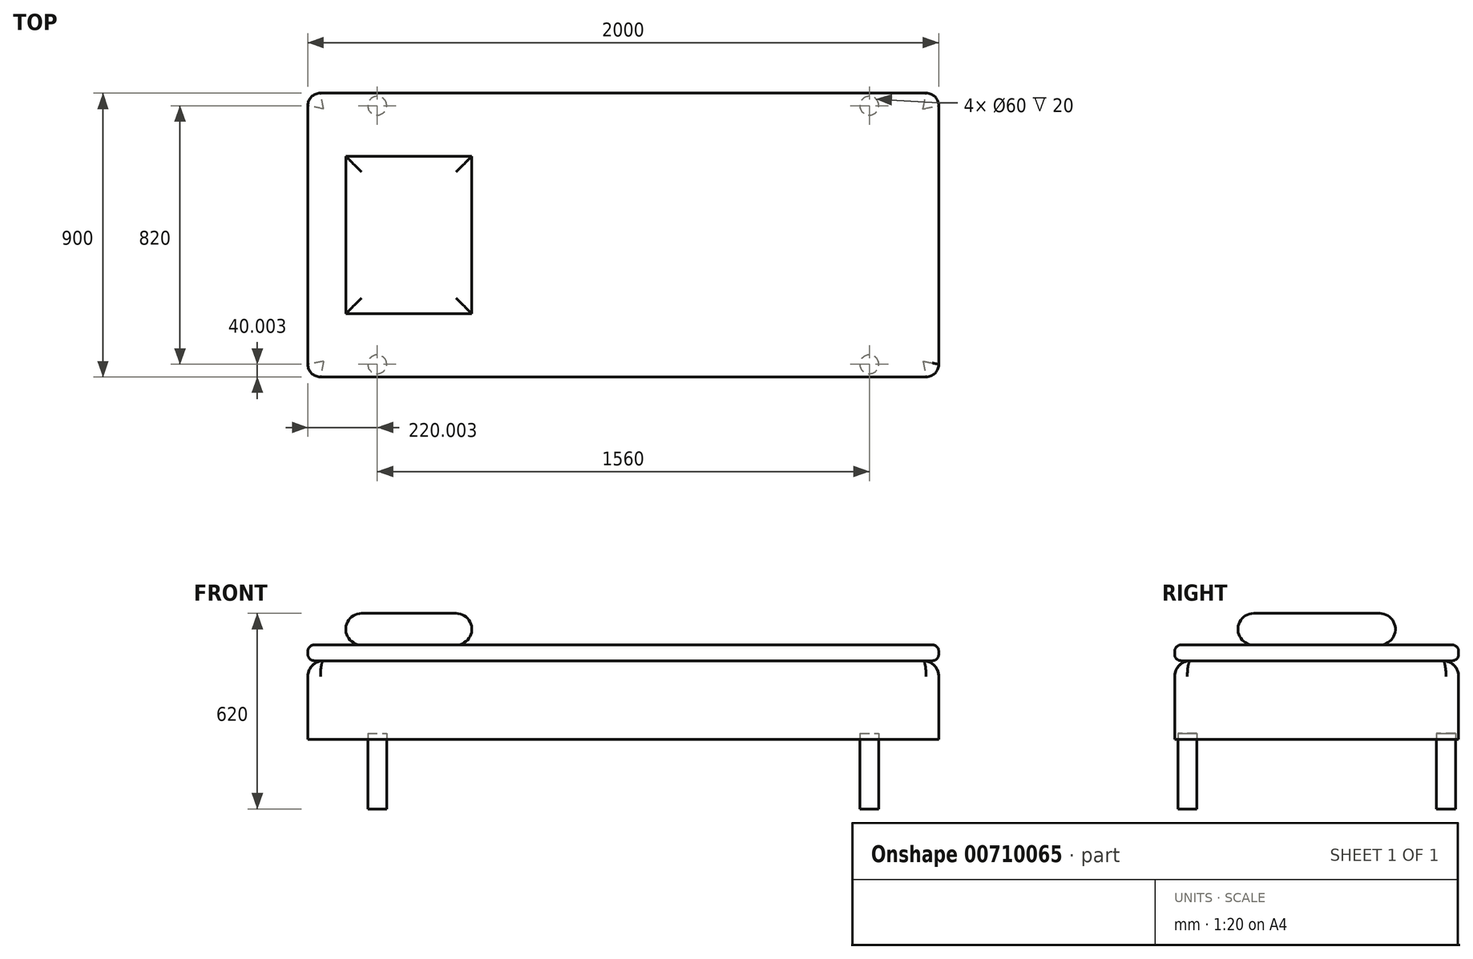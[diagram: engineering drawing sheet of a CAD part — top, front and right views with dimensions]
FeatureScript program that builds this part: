
annotation { "Feature Type Name" : "Feature", "Feature Type Description" : "" }
export const myFeature = defineFeature(function(context is Context, id is Id, definition is map)
    precondition{}
    {
        {
            var Q0;
            Q0=qCreatedBy(makeId("Top.planeOp"),FACE);
            var sketch = newSketch(context, id + "F0", { "sketchPlane" : qUnion([Q0])});
            skLineSegment(sketch, "E0.bottom", {"start": v(-1938.52, 970.76) * mm, "end": v(-18.52, 970.76) * mm});
            skLineSegment(sketch, "E0.top", {"start": v(-1938.52, 70.76) * mm, "end": v(-18.52, 70.76) * mm});
            skLineSegment(sketch, "E0.left", {"start": v(-1978.52, 930.76) * mm, "end": v(-1978.52, 110.76) * mm});
            skLineSegment(sketch, "E0.right", {"start": v(21.48, 930.76) * mm, "end": v(21.48, 110.76) * mm});
            skPoint(sketch, "E1.visualSharp", {"position": v(-1978.52, 970.76) * mm});
            skArc(sketch, "E1.filletArc", {"start": v(-1938.52, 970.76) * mm, "mid": v(-1966.8, 959.05) * mm, "end": v(-1978.52, 930.76) * mm});
            skPoint(sketch, "E2.visualSharp", {"position": v(-1978.52, 70.76) * mm});
            skArc(sketch, "E2.filletArc", {"start": v(-1978.52, 110.76) * mm, "mid": v(-1966.8, 82.48) * mm, "end": v(-1938.52, 70.76) * mm});
            skPoint(sketch, "E3.visualSharp", {"position": v(21.48, 70.76) * mm});
            skArc(sketch, "E3.filletArc", {"start": v(-18.52, 70.76) * mm, "mid": v(9.77, 82.48) * mm, "end": v(21.48, 110.76) * mm});
            skPoint(sketch, "E4.visualSharp", {"position": v(21.48, 970.76) * mm});
            skArc(sketch, "E4.filletArc", {"start": v(21.48, 930.76) * mm, "mid": v(9.77, 959.05) * mm, "end": v(-18.52, 970.76) * mm});
            skSolve(sketch);
        }
        {
            var Q0;
            Q0 = qSketchRegion(id + "F0", true);
            extrude(context, id + "F1", {"entities" : qUnion([Q0]), "depth" : 250 * mm, "offsetDistance" : 25 * mm});
        }
        {
            var Q0;
            Q0=makeQuery(id+"F1.opExtrude","CAP_EDGE",EDGE,{"disambiguationData":[OSD([sQuery(id+"F0.wireOp",EDGE,"E0.bottom")])],"isStart":false});
            fillet(context, id + "F2", {"entities" : qUnion([Q0]), "radius" : 50 * mm, "tangentPropagation" : true, "allowEdgeOverflow" : false});
        }
        {
            var Q0;
            Q0=makeQuery(id+"F1.opExtrude","CAP_FACE",FACE,{"disambiguationData":[OSD([sQuery(id+"F0.wireOp",EDGE,"E0.bottom"),sQuery(id+"F0.wireOp",EDGE,"E0.top"),sQuery(id+"F0.wireOp",EDGE,"E0.left"),sQuery(id+"F0.wireOp",EDGE,"E0.right"),sQuery(id+"F0.wireOp",EDGE,"E1.filletArc"),sQuery(id+"F0.wireOp",EDGE,"E2.filletArc"),sQuery(id+"F0.wireOp",EDGE,"E3.filletArc"),sQuery(id+"F0.wireOp",EDGE,"E4.filletArc")])],"isStart":true});
            var sketch = newSketch(context, id + "F3", { "sketchPlane" : qUnion([Q0])});
            skCircle(sketch, "E5", {"center": v(-1758.52, -110.76) * mm, "radius": 30 * mm});
            skLineSegment(sketch, "E6", {"start": v(-1758.52, -70.76) * mm, "end": v(-1758.52, -110.76) * mm, "construction": true});
            skLineSegment(sketch, "E7", {"start": v(-1758.52, -110.76) * mm, "end": v(-1978.52, -110.76) * mm, "construction": true});
            skLineSegment(sketch, "E8", {"start": v(-1978.52, -520.76) * mm, "end": v(21.48, -520.76) * mm, "construction": true});
            skLineSegment(sketch, "E9", {"start": v(-978.52, -70.76) * mm, "end": v(-978.52, -970.76) * mm, "construction": true});
            skCircle(sketch, "E10.MirrorC", {"center": v(-1758.52, -930.76) * mm, "radius": 30 * mm});
            skCircle(sketch, "E11.MirrorC", {"center": v(-198.52, -930.76) * mm, "radius": 30 * mm});
            skCircle(sketch, "E12.MirrorC", {"center": v(-198.52, -110.76) * mm, "radius": 30 * mm});
            skSolve(sketch);
        }
        {
            var Q0;
            Q0 = qSketchRegion(id + "F3", true);
            extrude(context, id + "F4", {"entities" : qUnion([Q0]), "operationType" : NewBodyOperationType.REMOVE, "oppositeDirection" : true, "depth" : 20 * mm, "offsetDistance" : 25 * mm});
        }
        {
            var Q0;
            Q0=makeQuery(id+"F1.opExtrude","CAP_FACE",FACE,{"disambiguationData":[OSD([sQuery(id+"F0.wireOp",EDGE,"E0.bottom"),sQuery(id+"F0.wireOp",EDGE,"E0.top"),sQuery(id+"F0.wireOp",EDGE,"E0.left"),sQuery(id+"F0.wireOp",EDGE,"E0.right"),sQuery(id+"F0.wireOp",EDGE,"E1.filletArc"),sQuery(id+"F0.wireOp",EDGE,"E2.filletArc"),sQuery(id+"F0.wireOp",EDGE,"E3.filletArc"),sQuery(id+"F0.wireOp",EDGE,"E4.filletArc")])],"isStart":false});
            var sketch = newSketch(context, id + "F5", { "sketchPlane" : qUnion([Q0])});
            skLineSegment(sketch, "E13.0", {"start": v(-1938.52, 970.76) * mm, "end": v(-18.52, 970.76) * mm});
            skArc(sketch, "E13.1", {"start": v(-18.52, 970.76) * mm, "mid": v(9.77, 959.05) * mm, "end": v(21.48, 930.76) * mm});
            skLineSegment(sketch, "E13.2", {"start": v(21.48, 930.76) * mm, "end": v(21.48, 110.76) * mm});
            skArc(sketch, "E13.3", {"start": v(21.48, 110.76) * mm, "mid": v(9.77, 82.48) * mm, "end": v(-18.52, 70.76) * mm});
            skLineSegment(sketch, "E13.4", {"start": v(-18.52, 70.76) * mm, "end": v(-1938.52, 70.76) * mm});
            skArc(sketch, "E13.5", {"start": v(-1938.52, 70.76) * mm, "mid": v(-1966.8, 82.48) * mm, "end": v(-1978.52, 110.76) * mm});
            skLineSegment(sketch, "E13.6", {"start": v(-1978.52, 110.76) * mm, "end": v(-1978.52, 930.76) * mm});
            skArc(sketch, "E13.7", {"start": v(-1978.52, 930.76) * mm, "mid": v(-1966.8, 959.05) * mm, "end": v(-1938.52, 970.76) * mm});
            skSolve(sketch);
        }
        {
            var Q0;
            Q0 = qSketchRegion(id + "F5", true);
            extrude(context, id + "F6", {"entities" : qUnion([Q0]), "depth" : 50 * mm, "offsetDistance" : 25 * mm});
        }
        {
            var Q0;
            Q0=makeQuery(id+"F6.opExtrude","CAP_EDGE",EDGE,{"disambiguationData":[OSD([sQuery(id+"F5.wireOp",EDGE,"E13.4")])],"isStart":false});
            var Q1;
            Q1=makeQuery(id+"F6.opExtrude","CAP_EDGE",EDGE,{"disambiguationData":[OSD([sQuery(id+"F5.wireOp",EDGE,"E13.4")])],"isStart":true});
            fillet(context, id + "F7", {"entities" : qUnion([Q0, Q1]), "radius" : 20 * mm, "tangentPropagation" : true, "allowEdgeOverflow" : false});
        }
        {
            var Q0;
            Q0 = qSketchRegion(id + "F3", true);
            extrude(context, id + "F8", {"entities" : qUnion([Q0]), "flatOperationType" : FlatOperationType.REMOVE, "depth" : 220 * mm, "offsetDistance" : 25 * mm, "domain" : OperationDomain.MODEL});
        }
        {
            var Q0;
            Q0=makeQuery(id+"F6.opExtrude","CAP_FACE",FACE,{"disambiguationData":[OSD([sQuery(id+"F5.wireOp",EDGE,"E13.0"),sQuery(id+"F5.wireOp",EDGE,"E13.1"),sQuery(id+"F5.wireOp",EDGE,"E13.2"),sQuery(id+"F5.wireOp",EDGE,"E13.3"),sQuery(id+"F5.wireOp",EDGE,"E13.4"),sQuery(id+"F5.wireOp",EDGE,"E13.5"),sQuery(id+"F5.wireOp",EDGE,"E13.6"),sQuery(id+"F5.wireOp",EDGE,"E13.7")])],"isStart":false});
            var sketch = newSketch(context, id + "F9", { "sketchPlane" : qUnion([Q0])});
            skLineSegment(sketch, "E14.bottom", {"start": v(-1858.52, 770.76) * mm, "end": v(-1458.52, 770.76) * mm});
            skLineSegment(sketch, "E14.top", {"start": v(-1858.52, 270.76) * mm, "end": v(-1458.52, 270.76) * mm});
            skLineSegment(sketch, "E14.left", {"start": v(-1858.52, 770.76) * mm, "end": v(-1858.52, 270.76) * mm});
            skLineSegment(sketch, "E14.right", {"start": v(-1458.52, 770.76) * mm, "end": v(-1458.52, 270.76) * mm});
            skLineSegment(sketch, "E15", {"start": v(-1858.52, 520.76) * mm, "end": v(-1958.52, 520.76) * mm, "construction": true});
            skSolve(sketch);
        }
        {
            var Q0;
            Q0=makeQuery(id+"F9.imprint","IMPRINT",FACE,{"disambiguationData":[TD([[makeQuery(id+"F9.imprint","IMPRINT",EDGE,{"derivedFrom":sQuery(id+"F9.wireOp",EDGE,"E14.bottom")}),-1.0]])]});
            extrude(context, id + "F10", {"entities" : qUnion([Q0]), "depth" : 100 * mm, "offsetDistance" : 25 * mm});
        }
        {
            var Q0;
            Q0=makeQuery(id+"F10.opExtrude","CAP_EDGE",EDGE,{"disambiguationData":[OSD([sQuery(id+"F9.wireOp",EDGE,"E14.left")])],"isStart":false});
            var Q1;
            Q1=makeQuery(id+"F10.opExtrude","CAP_EDGE",EDGE,{"disambiguationData":[OSD([sQuery(id+"F9.wireOp",EDGE,"E14.right")])],"isStart":false});
            var Q2;
            Q2=makeQuery(id+"F10.opExtrude","CAP_EDGE",EDGE,{"disambiguationData":[OSD([sQuery(id+"F9.wireOp",EDGE,"E14.top")])],"isStart":false});
            var Q3;
            Q3=makeQuery(id+"F10.opExtrude","CAP_EDGE",EDGE,{"disambiguationData":[OSD([sQuery(id+"F9.wireOp",EDGE,"E14.bottom")])],"isStart":false});
            var Q4;
            Q4=makeQuery(id+"F10.opExtrude","CAP_EDGE",EDGE,{"disambiguationData":[OSD([sQuery(id+"F9.wireOp",EDGE,"E14.top")])],"isStart":true});
            var Q5;
            Q5=makeQuery(id+"F10.opExtrude","CAP_EDGE",EDGE,{"disambiguationData":[OSD([sQuery(id+"F9.wireOp",EDGE,"E14.left")])],"isStart":true});
            var Q6;
            Q6=makeQuery(id+"F10.opExtrude","CAP_EDGE",EDGE,{"disambiguationData":[OSD([sQuery(id+"F9.wireOp",EDGE,"E14.right")])],"isStart":true});
            var Q7;
            Q7=makeQuery(id+"F10.opExtrude","CAP_EDGE",EDGE,{"disambiguationData":[OSD([sQuery(id+"F9.wireOp",EDGE,"E14.bottom")])],"isStart":true});
            fillet(context, id + "F11", {"entities" : qUnion([Q0, Q1, Q2, Q3, Q4, Q5, Q6, Q7]), "radius" : 50 * mm, "tangentPropagation" : true, "allowEdgeOverflow" : false});
        }
    });
